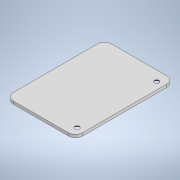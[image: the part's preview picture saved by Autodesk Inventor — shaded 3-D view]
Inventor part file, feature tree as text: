
AUTODESK INVENTOR PART (.ipt)
format: ipt  version: 2021.2 (Build 252289000, 289)  size: 117,248 bytes
history: native  units: mm
features: extrude x2, sketch x2, other x1, chamfer x1
ambient origin geometry x8: Origin, YZ Plane, XZ Plane, XY Plane, X Axis, Y Axis, Z Axis, Center Point
bodies: Body1 (feature_tree)
feature tree (6):
  other  "Твердое тело1"
  extrude  "Выдавливание1"  Depth=68.0mm
  extrude  "Выдавливание2"  Depth=48.0mm
  chamfer  "Фаска1"  Distance=5.0mm
  sketch  "Эскиз1"
  sketch  "Эскиз2"
